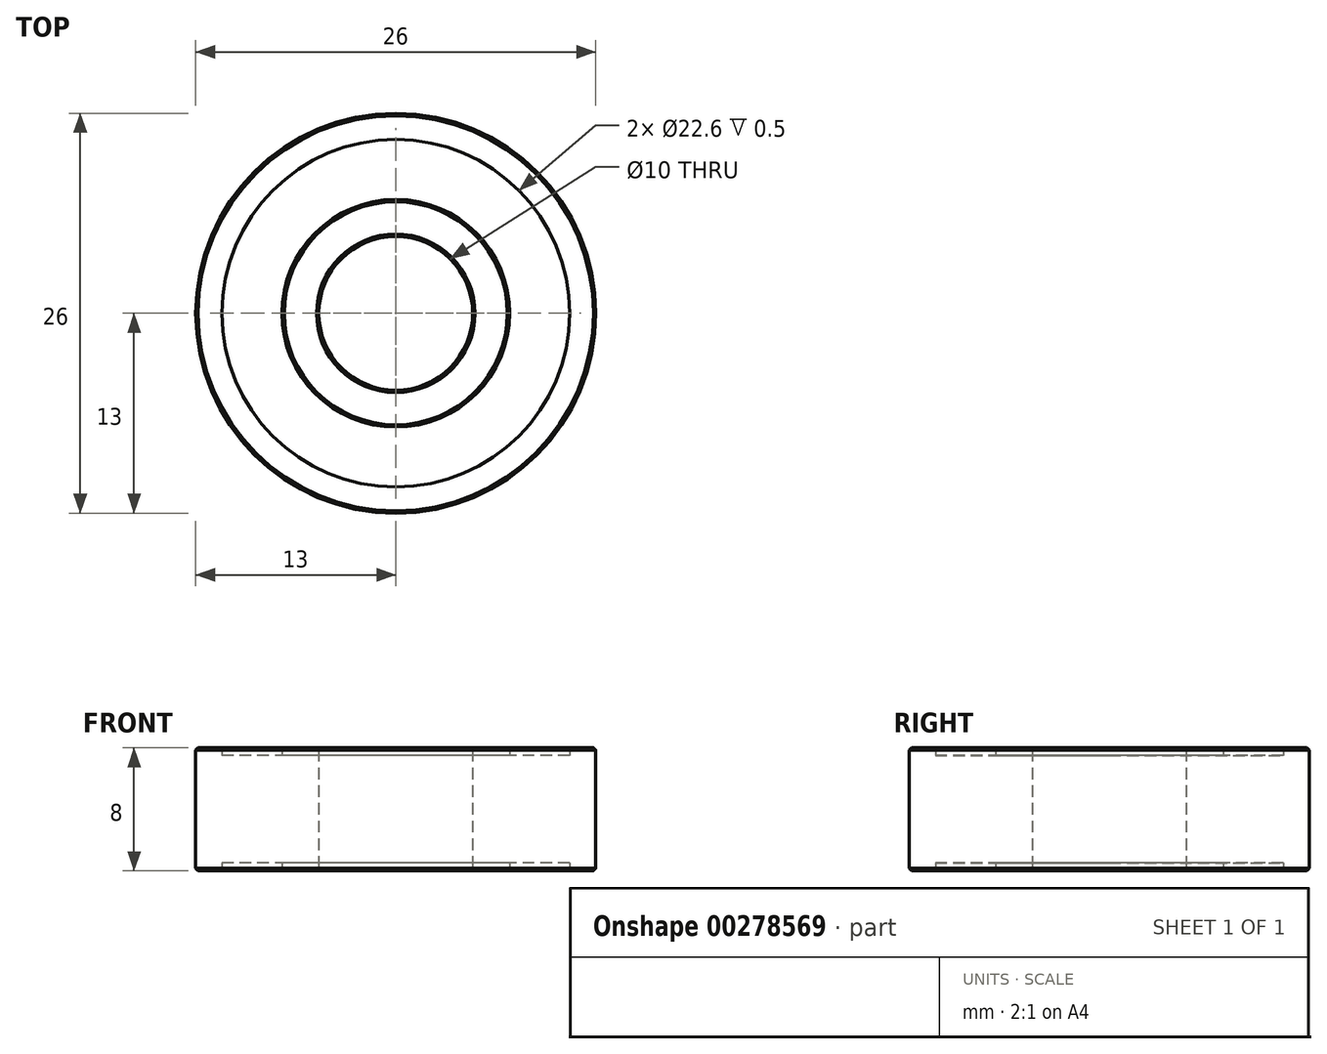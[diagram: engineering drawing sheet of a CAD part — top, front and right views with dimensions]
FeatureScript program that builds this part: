
annotation { "Feature Type Name" : "Feature", "Feature Type Description" : "" }
export const myFeature = defineFeature(function(context is Context, id is Id, definition is map)
    precondition{}
    {
        {
            var Q0;
            Q0=qCreatedBy(makeId("Top.planeOp"),FACE);
            var sketch = newSketch(context, id + "F0", { "sketchPlane" : qUnion([Q0])});
            skCircle(sketch, "E0", {"center": v(0, 0) * mm, "radius": 5 * mm});
            skCircle(sketch, "E1", {"center": v(0, 0) * mm, "radius": 13 * mm});
            skCircle(sketch, "E2", {"center": v(0, 0) * mm, "radius": 7.4 * mm});
            skCircle(sketch, "E3", {"center": v(0, 0) * mm, "radius": 11.3 * mm});
            skSolve(sketch);
        }
        {
            var Q0;
            Q0=makeQuery(id+"F0.imprint","IMPRINT",FACE,{"disambiguationData":[TD([[makeQuery(id+"F0.imprint","IMPRINT",EDGE,{"derivedFrom":sQuery(id+"F0.wireOp",EDGE,"E0")}),-1.0]])]});
            var Q1;
            Q1=makeQuery(id+"F0.imprint","IMPRINT",FACE,{"disambiguationData":[TD([[makeQuery(id+"F0.imprint","IMPRINT",EDGE,{"derivedFrom":sQuery(id+"F0.wireOp",EDGE,"E1")}),1.0]])]});
            var Q2;
            Q2=makeQuery(id+"F0.imprint","IMPRINT",FACE,{"disambiguationData":[TD([[makeQuery(id+"F0.imprint","IMPRINT",EDGE,{"derivedFrom":sQuery(id+"F0.wireOp",EDGE,"E2")}),-1.0]])]});
            extrude(context, id + "F1", {"entities" : qUnion([Q0, Q1, Q2]), "depth" : 8 * mm});
        }
        {
            var Q0;
            Q0=makeQuery(id+"F0.imprint","IMPRINT",FACE,{"disambiguationData":[TD([[makeQuery(id+"F0.imprint","IMPRINT",EDGE,{"derivedFrom":sQuery(id+"F0.wireOp",EDGE,"E2")}),-1.0]])]});
            extrude(context, id + "F2", {"entities" : qUnion([Q0]), "operationType" : NewBodyOperationType.REMOVE, "depth" : 0.5 * mm});
        }
        {
            var Q0;
            Q0=makeQuery(id+"F0.imprint","IMPRINT",FACE,{"disambiguationData":[TD([[makeQuery(id+"F0.imprint","IMPRINT",EDGE,{"derivedFrom":sQuery(id+"F0.wireOp",EDGE,"E2")}),-1.0]])]});
            extrude(context, id + "F3", {"entities" : qUnion([Q0]), "operationType" : NewBodyOperationType.REMOVE, "depth" : 8 * mm, "hasSecondDirection" : true, "secondDirectionOppositeDirection" : false, "secondDirectionDepth" : 7.5 * mm});
        }
        {
            var Q0;
            Q0=makeQuery(id+"F1.opExtrude","CAP_EDGE",EDGE,{"disambiguationData":[OSD([sQuery(id+"F0.wireOp",EDGE,"E1")])],"isStart":true});
            var Q1;
            Q1=makeQuery(id+"F2.boolean.opBoolean","COPY",EDGE,{"derivedFrom":makeQuery(id+"F2.opExtrude","CAP_EDGE",EDGE,{"disambiguationData":[OSD([sQuery(id+"F0.wireOp",EDGE,"E3")])],"isStart":true})});
            var Q2;
            Q2=makeQuery(id+"F2.boolean.opBoolean","COPY",EDGE,{"derivedFrom":makeQuery(id+"F2.opExtrude","CAP_EDGE",EDGE,{"disambiguationData":[OSD([sQuery(id+"F0.wireOp",EDGE,"E2")])],"isStart":true})});
            var Q3;
            Q3=makeQuery(id+"F1.opExtrude","CAP_EDGE",EDGE,{"disambiguationData":[OSD([sQuery(id+"F0.wireOp",EDGE,"E0")])],"isStart":true});
            var Q4;
            Q4=makeQuery(id+"F1.opExtrude","CAP_EDGE",EDGE,{"disambiguationData":[OSD([sQuery(id+"F0.wireOp",EDGE,"E1")])],"isStart":false});
            var Q5;
            Q5=makeQuery(id+"F3.boolean.opBoolean","COPY",EDGE,{"derivedFrom":makeQuery(id+"F3.opExtrude","CAP_EDGE",EDGE,{"disambiguationData":[OSD([sQuery(id+"F0.wireOp",EDGE,"E3")])],"isStart":false})});
            var Q6;
            Q6=makeQuery(id+"F3.boolean.opBoolean","COPY",EDGE,{"derivedFrom":makeQuery(id+"F3.opExtrude","CAP_EDGE",EDGE,{"disambiguationData":[OSD([sQuery(id+"F0.wireOp",EDGE,"E2")])],"isStart":false})});
            var Q7;
            Q7=makeQuery(id+"F1.opExtrude","CAP_EDGE",EDGE,{"disambiguationData":[OSD([sQuery(id+"F0.wireOp",EDGE,"E0")])],"isStart":false});
            chamfer(context, id + "F4", {"entities" : qUnion([Q0, Q1, Q2, Q3, Q4, Q5, Q6, Q7]), "width" : .15 * mm, "tangentPropagation" : true});
        }
    });
